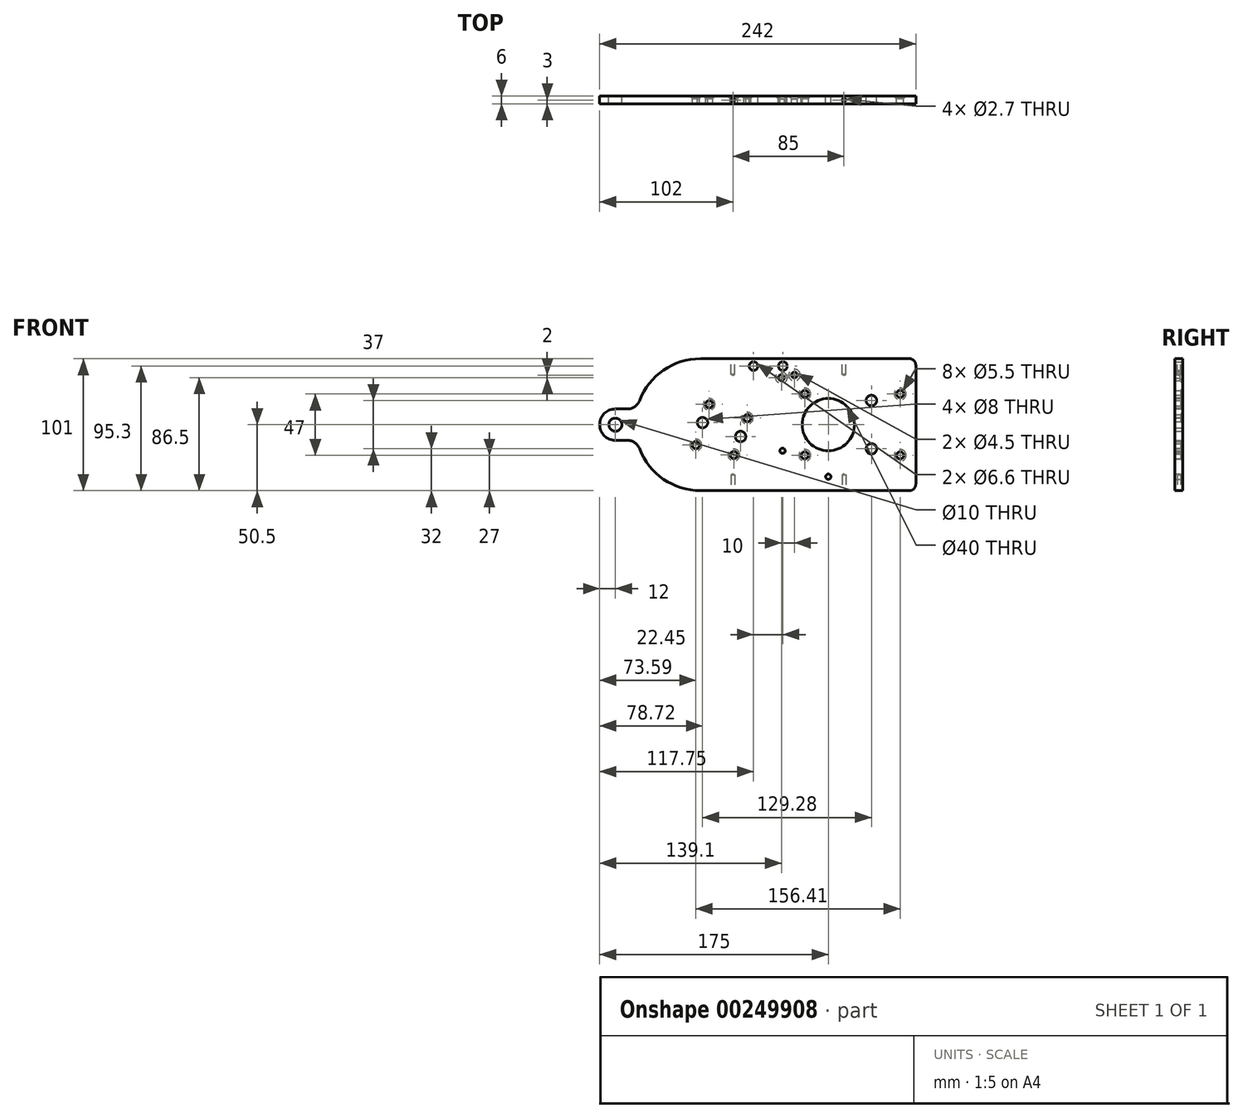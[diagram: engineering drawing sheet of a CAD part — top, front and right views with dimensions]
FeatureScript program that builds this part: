
annotation { "Feature Type Name" : "Feature", "Feature Type Description" : "" }
export const myFeature = defineFeature(function(context is Context, id is Id, definition is map)
    precondition{}
    {
        {
            var Q0;
            Q0=qCreatedBy(makeId("Front.planeOp"),FACE);
            var sketch = newSketch(context, id + "F0", { "sketchPlane" : qUnion([Q0])});
            skLineSegment(sketch, "E0.bottom", {"start": v(-115, -50.5) * mm, "end": v(115, -50.5) * mm});
            skLineSegment(sketch, "E0.top", {"start": v(-49.78, 50.5) * mm, "end": v(115, 50.5) * mm});
            skLineSegment(sketch, "E0.left", {"start": v(-115, -50.5) * mm, "end": v(-115, -12) * mm});
            skLineSegment(sketch, "E0.right", {"start": v(115, -50.5) * mm, "end": v(115, 50.5) * mm});
            skLineSegment(sketch, "E1", {"start": v(-162.21, 0) * mm, "end": v(164.39, 0) * mm, "construction": true});
            skPoint(sketch, "E1.endSnap0", {"position": v(115, 0) * mm});
            skCircle(sketch, "E2", {"center": v(-115, 0) * mm, "radius": 5 * mm});
            skArc(sketch, "E3", {"start": v(-115, 12) * mm, "mid": v(-127, 0) * mm, "end": v(-115, -12) * mm});
            skLineSegment(sketch, "E4", {"start": v(-115, 12) * mm, "end": v(-105.8, 12) * mm});
            skLineSegment(sketch, "E5", {"start": v(-115, -12) * mm, "end": v(-105.8, -12) * mm});
            skArc(sketch, "E6", {"start": v(-105.8, 12) * mm, "mid": v(-100.14, 13.76) * mm, "end": v(-96.46, 18.42) * mm});
            skArc(sketch, "E7", {"start": v(-96.46, 18.42) * mm, "mid": v(-78.1, 41.7) * mm, "end": v(-49.78, 50.5) * mm});
            skArc(sketch, "E8", {"start": v(-105.8, -12) * mm, "mid": v(-100.14, -13.76) * mm, "end": v(-96.46, -18.42) * mm});
            skArc(sketch, "E9", {"start": v(-96.46, -18.42) * mm, "mid": v(-78.1, -41.7) * mm, "end": v(-49.78, -50.5) * mm});
            skPoint(sketch, "E10.orphan", {"position": v(-115, 50.5) * mm});
            skCircle(sketch, "E11", {"center": v(48, 0) * mm, "radius": 20 * mm});
            skCircle(sketch, "E12", {"center": v(81, -18.5) * mm, "radius": 4 * mm});
            skCircle(sketch, "E13", {"center": v(81, 18.5) * mm, "radius": 4 * mm});
            skLineSegment(sketch, "E14", {"start": v(103, 65.88) * mm, "end": v(103, -57.13) * mm, "construction": true});
            skCircle(sketch, "E15", {"center": v(103, -23.5) * mm, "radius": 3.48 * mm});
            skCircle(sketch, "E16", {"center": v(103, 23.5) * mm, "radius": 3.5 * mm});
            skCircle(sketch, "E17", {"center": v(30, 23.5) * mm, "radius": 6.97 * mm});
            skCircle(sketch, "E18", {"center": v(30, -23.5) * mm, "radius": 11.5 * mm});
            skCircle(sketch, "E19", {"center": v(-48.28, 1.52) * mm, "radius": 4 * mm});
            skCircle(sketch, "E20", {"center": v(-19.15, -9.1) * mm, "radius": 4 * mm});
            skCircle(sketch, "E21", {"center": v(-14.02, 5) * mm, "radius": 5.47 * mm});
            skCircle(sketch, "E22", {"center": v(-24.28, -23.2) * mm, "radius": 5.45 * mm});
            skCircle(sketch, "E23", {"center": v(-43.15, 15.6) * mm, "radius": 4.25 * mm});
            skCircle(sketch, "E24", {"center": v(-53.41, -15.6) * mm, "radius": 6.02 * mm});
            skCircle(sketch, "E25", {"center": v(22.1, 38) * mm, "radius": 6.15 * mm});
            skCircle(sketch, "E26", {"center": v(12.1, 36) * mm, "radius": 7.66 * mm});
            skCircle(sketch, "E27", {"center": v(48, -39.8) * mm, "radius": 2 * mm});
            skCircle(sketch, "E28", {"center": v(13, -20) * mm, "radius": 2 * mm});
            skCircle(sketch, "E29", {"center": v(13.2, 44.8) * mm, "radius": 2.64 * mm});
            skCircle(sketch, "E30", {"center": v(-9.25, 44.8) * mm, "radius": 3.14 * mm});
            skSolve(sketch);
        }
        {
            var Q0;
            Q0=makeQuery(id+"F0.imprint","IMPRINT",FACE,{"disambiguationData":[TD([[makeQuery(id+"F0.imprint","IMPRINT",EDGE,{"derivedFrom":sQuery(id+"F0.wireOp",EDGE,"E0.top")}),-1.0]])]});
            var Q1;
            Q1=makeQuery(id+"F0.imprint","IMPRINT",FACE,{"disambiguationData":[TD([[makeQuery(id+"F0.imprint","IMPRINT",EDGE,{"derivedFrom":sQuery(id+"F0.wireOp",EDGE,"E23")}),1.0]])]});
            var Q2;
            Q2=makeQuery(id+"F0.imprint","IMPRINT",FACE,{"disambiguationData":[TD([[makeQuery(id+"F0.imprint","IMPRINT",EDGE,{"derivedFrom":sQuery(id+"F0.wireOp",EDGE,"E24")}),1.0]])]});
            var Q3;
            Q3=makeQuery(id+"F0.imprint","IMPRINT",FACE,{"disambiguationData":[TD([[makeQuery(id+"F0.imprint","IMPRINT",EDGE,{"derivedFrom":sQuery(id+"F0.wireOp",EDGE,"E21")}),1.0]])]});
            var Q4;
            Q4=makeQuery(id+"F0.imprint","IMPRINT",FACE,{"disambiguationData":[TD([[makeQuery(id+"F0.imprint","IMPRINT",EDGE,{"derivedFrom":sQuery(id+"F0.wireOp",EDGE,"E22")}),1.0]])]});
            var Q5;
            {var subQ0=sQuery(id+"F0.wireOp",EDGE,"E26");var subQ1=sQuery(id+"F0.wireOp",EDGE,"E25");var subQ2=makeQuery(id+"F0.imprint","INTERSECT",VERTEX,{"disambiguationData":[OD(0.0)],"derivedFrom":[subQ1,subQ0]});Q5=makeQuery(id+"F0.imprint","IMPRINT",FACE,{"disambiguationData":[TD([[makeQuery(id+"F0.imprint","IMPRINT",EDGE,{"disambiguationData":[TD([[subQ2,-1.0]])],"derivedFrom":subQ1}),-1.0]])]});}
            var Q6;
            {var subQ0=sQuery(id+"F0.wireOp",EDGE,"E26");var subQ1=sQuery(id+"F0.wireOp",EDGE,"E25");var subQ2=makeQuery(id+"F0.imprint","INTERSECT",VERTEX,{"disambiguationData":[OD(0.0)],"derivedFrom":[subQ1,subQ0]});Q6=makeQuery(id+"F0.imprint","IMPRINT",FACE,{"disambiguationData":[TD([[makeQuery(id+"F0.imprint","IMPRINT",EDGE,{"disambiguationData":[TD([[subQ2,1.0]])],"derivedFrom":subQ1}),1.0]])]});}
            var Q7;
            Q7=makeQuery(id+"F0.imprint","IMPRINT",FACE,{"disambiguationData":[TD([[makeQuery(id+"F0.imprint","IMPRINT",EDGE,{"derivedFrom":sQuery(id+"F0.wireOp",EDGE,"E17")}),1.0]])]});
            var Q8;
            {var subQ0=sQuery(id+"F0.wireOp",EDGE,"E18");var subQ1=sQuery(id+"F0.wireOp",EDGE,"E11");var subQ2=makeQuery(id+"F0.imprint","INTERSECT",VERTEX,{"disambiguationData":[OD(0.0)],"derivedFrom":[subQ1,subQ0]});Q8=makeQuery(id+"F0.imprint","IMPRINT",FACE,{"disambiguationData":[TD([[makeQuery(id+"F0.imprint","IMPRINT",EDGE,{"disambiguationData":[TD([[subQ2,-1.0]])],"derivedFrom":subQ1}),-1.0]])]});}
            var Q9;
            Q9=makeQuery(id+"F0.imprint","IMPRINT",FACE,{"disambiguationData":[TD([[makeQuery(id+"F0.imprint","IMPRINT",EDGE,{"derivedFrom":sQuery(id+"F0.wireOp",EDGE,"E16")}),1.0]])]});
            var Q10;
            Q10=makeQuery(id+"F0.imprint","IMPRINT",FACE,{"disambiguationData":[TD([[makeQuery(id+"F0.imprint","IMPRINT",EDGE,{"derivedFrom":sQuery(id+"F0.wireOp",EDGE,"E15")}),1.0]])]});
            var Q11;
            {var subQ0=sQuery(id+"F0.wireOp",EDGE,"E29");var subQ1=sQuery(id+"F0.wireOp",EDGE,"E26");var subQ2=makeQuery(id+"F0.imprint","INTERSECT",VERTEX,{"disambiguationData":[OD(0.0)],"derivedFrom":[subQ1,subQ0]});Q11=makeQuery(id+"F0.imprint","IMPRINT",FACE,{"disambiguationData":[TD([[makeQuery(id+"F0.imprint","IMPRINT",EDGE,{"disambiguationData":[TD([[subQ2,-1.0]])],"derivedFrom":subQ1}),-1.0]])]});}
            var Q12;
            {var subQ0=sQuery(id+"F0.wireOp",EDGE,"E29");var subQ1=sQuery(id+"F0.wireOp",EDGE,"E26");var subQ2=makeQuery(id+"F0.imprint","INTERSECT",VERTEX,{"disambiguationData":[OD(0.0)],"derivedFrom":[subQ1,subQ0]});Q12=makeQuery(id+"F0.imprint","IMPRINT",FACE,{"disambiguationData":[TD([[makeQuery(id+"F0.imprint","IMPRINT",EDGE,{"disambiguationData":[TD([[subQ2,-1.0]])],"derivedFrom":subQ1}),1.0]])]});}
            var Q13;
            Q13=makeQuery(id+"F0.imprint","IMPRINT",FACE,{"disambiguationData":[TD([[makeQuery(id+"F0.imprint","IMPRINT",EDGE,{"derivedFrom":sQuery(id+"F0.wireOp",EDGE,"E30")}),1.0]])]});
            var Q14;
            {var subQ0=sQuery(id+"F0.wireOp",EDGE,"E26");var subQ1=sQuery(id+"F0.wireOp",EDGE,"E25");var subQ2=makeQuery(id+"F0.imprint","INTERSECT",VERTEX,{"disambiguationData":[OD(0.0)],"derivedFrom":[subQ1,subQ0]});Q14=makeQuery(id+"F0.imprint","IMPRINT",FACE,{"disambiguationData":[TD([[makeQuery(id+"F0.imprint","IMPRINT",EDGE,{"disambiguationData":[TD([[subQ2,-1.0]])],"derivedFrom":subQ1}),1.0]])]});}
            extrude(context, id + "F1", {"entities" : qUnion([Q0, Q1, Q2, Q3, Q4, Q5, Q6, Q7, Q8, Q9, Q10, Q11, Q12, Q13, Q14]), "depth" : 6 * mm});
        }
        {
            var Q0;
            Q0=sQuery(id+"F0.wireOp",VERTEX,"E23.center");
            var Q1;
            Q1=sQuery(id+"F0.wireOp",VERTEX,"E24.center");
            var Q2;
            Q2=sQuery(id+"F0.wireOp",VERTEX,"E21.center");
            var Q3;
            Q3=sQuery(id+"F0.wireOp",VERTEX,"E22.center");
            var Q4;
            Q4=sQuery(id+"F0.wireOp",VERTEX,"E18.center");
            var Q5;
            Q5=sQuery(id+"F0.wireOp",VERTEX,"E17.center");
            var Q6;
            Q6=sQuery(id+"F0.wireOp",VERTEX,"E16.center");
            var Q7;
            Q7=sQuery(id+"F0.wireOp",VERTEX,"E15.center");
            var Q8;
            Q8=makeQuery(id+"F1.opExtrude","SWEPT_BODY",BODY,{"disambiguationData":[OSD([sQuery(id+"F0.wireOp",EDGE,"E0.bottom"),sQuery(id+"F0.wireOp",EDGE,"E0.top"),sQuery(id+"F0.wireOp",EDGE,"E0.right"),sQuery(id+"F0.wireOp",EDGE,"E2"),sQuery(id+"F0.wireOp",EDGE,"E3"),sQuery(id+"F0.wireOp",EDGE,"E4"),sQuery(id+"F0.wireOp",EDGE,"E5"),sQuery(id+"F0.wireOp",EDGE,"E6"),sQuery(id+"F0.wireOp",EDGE,"E7"),sQuery(id+"F0.wireOp",EDGE,"E8"),sQuery(id+"F0.wireOp",EDGE,"E9"),sQuery(id+"F0.wireOp",EDGE,"E11"),sQuery(id+"F0.wireOp",EDGE,"E12"),sQuery(id+"F0.wireOp",EDGE,"E13"),sQuery(id+"F0.wireOp",EDGE,"E19"),sQuery(id+"F0.wireOp",EDGE,"E20"),sQuery(id+"F0.wireOp",EDGE,"E27"),sQuery(id+"F0.wireOp",EDGE,"E28")])]});
            hole(context, id + "F2", {"style" : HoleStyle.C_SINK, "endStyle" : HoleEndStyle.THROUGH, "oppositeDirection" : true, "holeDiameter" : 5.5 * mm, "cSinkDiameter" : 8.96 * mm, "cSinkAngle" : 90 * degree, "tappedDepth" : 12 * mm, "tapClearance" : 3, "locations" : qUnion([Q0, Q1, Q2, Q3, Q4, Q5, Q6, Q7]), "scope" : qUnion([Q8])});
        }
        {
            var Q0;
            Q0=sQuery(id+"F0.wireOp",VERTEX,"E25.center");
            var Q1;
            Q1=sQuery(id+"F0.wireOp",VERTEX,"E26.center");
            var Q2;
            Q2=makeQuery(id+"F1.opExtrude","SWEPT_BODY",BODY,{"disambiguationData":[OSD([sQuery(id+"F0.wireOp",EDGE,"E0.bottom"),sQuery(id+"F0.wireOp",EDGE,"E0.top"),sQuery(id+"F0.wireOp",EDGE,"E0.right"),sQuery(id+"F0.wireOp",EDGE,"E2"),sQuery(id+"F0.wireOp",EDGE,"E3"),sQuery(id+"F0.wireOp",EDGE,"E4"),sQuery(id+"F0.wireOp",EDGE,"E5"),sQuery(id+"F0.wireOp",EDGE,"E6"),sQuery(id+"F0.wireOp",EDGE,"E7"),sQuery(id+"F0.wireOp",EDGE,"E8"),sQuery(id+"F0.wireOp",EDGE,"E9"),sQuery(id+"F0.wireOp",EDGE,"E11"),sQuery(id+"F0.wireOp",EDGE,"E12"),sQuery(id+"F0.wireOp",EDGE,"E13"),sQuery(id+"F0.wireOp",EDGE,"E19"),sQuery(id+"F0.wireOp",EDGE,"E20"),sQuery(id+"F0.wireOp",EDGE,"E27"),sQuery(id+"F0.wireOp",EDGE,"E28")])]});
            hole(context, id + "F3", {"style" : HoleStyle.C_SINK, "endStyle" : HoleEndStyle.THROUGH, "oppositeDirection" : true, "holeDiameter" : 4.5 * mm, "cSinkDiameter" : 8.96 * mm, "cSinkAngle" : 90 * degree, "tappedDepth" : 12 * mm, "tapClearance" : 3, "locations" : qUnion([Q0, Q1]), "scope" : qUnion([Q2])});
        }
        {
            var Q0;
            Q0=sQuery(id+"F0.wireOp",VERTEX,"E30.center");
            var Q1;
            Q1=sQuery(id+"F0.wireOp",VERTEX,"E29.center");
            var Q2;
            Q2=makeQuery(id+"F1.opExtrude","SWEPT_BODY",BODY,{"disambiguationData":[OSD([sQuery(id+"F0.wireOp",EDGE,"E0.bottom"),sQuery(id+"F0.wireOp",EDGE,"E0.top"),sQuery(id+"F0.wireOp",EDGE,"E0.right"),sQuery(id+"F0.wireOp",EDGE,"E2"),sQuery(id+"F0.wireOp",EDGE,"E3"),sQuery(id+"F0.wireOp",EDGE,"E4"),sQuery(id+"F0.wireOp",EDGE,"E5"),sQuery(id+"F0.wireOp",EDGE,"E6"),sQuery(id+"F0.wireOp",EDGE,"E7"),sQuery(id+"F0.wireOp",EDGE,"E8"),sQuery(id+"F0.wireOp",EDGE,"E9"),sQuery(id+"F0.wireOp",EDGE,"E11"),sQuery(id+"F0.wireOp",EDGE,"E12"),sQuery(id+"F0.wireOp",EDGE,"E13"),sQuery(id+"F0.wireOp",EDGE,"E19"),sQuery(id+"F0.wireOp",EDGE,"E20"),sQuery(id+"F0.wireOp",EDGE,"E27"),sQuery(id+"F0.wireOp",EDGE,"E28")])]});
            hole(context, id + "F4", {"style" : HoleStyle.SIMPLE, "endStyle" : HoleEndStyle.THROUGH, "oppositeDirection" : true, "standardTappedOrClearance" : lookupTablePath({ "standard" : "ISO", "fit" : "Normal", "size" : "M6", "type" : "Clearance" }), "standardBlindInLast" : lookupTablePath({ "fit" : "Standard", "standard" : "ISO", "size" : "M6", "type" : "Clearance" }), "holeDiameter" : 6.6 * mm, "tappedDepth" : 12 * mm, "tapClearance" : 3, "locations" : qUnion([Q0, Q1]), "scope" : qUnion([Q2])});
        }
        {
            var Q0;
            Q0=makeQuery(id+"F1.opExtrude","SWEPT_FACE",FACE,{"disambiguationData":[OSD([sQuery(id+"F0.wireOp",EDGE,"E0.bottom")])]});
            var sketch = newSketch(context, id + "F5", { "sketchPlane" : qUnion([Q0])});
            skLineSegment(sketch, "E31", {"start": v(-53.96, 3) * mm, "end": v(118.5, 3) * mm, "construction": true});
            skPoint(sketch, "E31.startSnap0", {"position": v(-49.78, 3) * mm});
            skPoint(sketch, "E32", {"position": v(60, 3) * mm});
            skPoint(sketch, "E33", {"position": v(-25, 3) * mm});
            skSolve(sketch);
        }
        {
            var Q0;
            Q0=sQuery(id+"F5.wireOp",VERTEX,"E32");
            var Q1;
            Q1=sQuery(id+"F5.wireOp",VERTEX,"E33");
            var Q2;
            Q2=makeQuery(id+"F1.opExtrude","SWEPT_BODY",BODY,{"disambiguationData":[OSD([sQuery(id+"F0.wireOp",EDGE,"E0.bottom"),sQuery(id+"F0.wireOp",EDGE,"E0.top"),sQuery(id+"F0.wireOp",EDGE,"E0.right"),sQuery(id+"F0.wireOp",EDGE,"E2"),sQuery(id+"F0.wireOp",EDGE,"E3"),sQuery(id+"F0.wireOp",EDGE,"E4"),sQuery(id+"F0.wireOp",EDGE,"E5"),sQuery(id+"F0.wireOp",EDGE,"E6"),sQuery(id+"F0.wireOp",EDGE,"E7"),sQuery(id+"F0.wireOp",EDGE,"E8"),sQuery(id+"F0.wireOp",EDGE,"E9"),sQuery(id+"F0.wireOp",EDGE,"E11"),sQuery(id+"F0.wireOp",EDGE,"E12"),sQuery(id+"F0.wireOp",EDGE,"E13"),sQuery(id+"F0.wireOp",EDGE,"E19"),sQuery(id+"F0.wireOp",EDGE,"E20"),sQuery(id+"F0.wireOp",EDGE,"E27"),sQuery(id+"F0.wireOp",EDGE,"E28")])]});
            hole(context, id + "F6", {"style" : HoleStyle.SIMPLE, "endStyle" : HoleEndStyle.BLIND, "holeDiameter" : 2.7 * mm, "holeDepth" : 12 * mm, "tappedDepth" : 12 * mm, "tapClearance" : 3, "locations" : qUnion([Q0, Q1]), "scope" : qUnion([Q2])});
        }
        {
            var Q0;
            Q0=makeQuery(id+"F1.opExtrude","SWEPT_FACE",FACE,{"disambiguationData":[OSD([sQuery(id+"F0.wireOp",EDGE,"E0.top")])]});
            var sketch = newSketch(context, id + "F7", { "sketchPlane" : qUnion([Q0])});
            skLineSegment(sketch, "E34", {"start": v(115, -3) * mm, "end": v(-65.1, -3) * mm, "construction": true});
            skPoint(sketch, "E35", {"position": v(60, -3) * mm});
            skPoint(sketch, "E36", {"position": v(-25, -3) * mm});
            skSolve(sketch);
        }
        {
            var Q0;
            Q0=sQuery(id+"F7.wireOp",VERTEX,"E36");
            var Q1;
            Q1=sQuery(id+"F7.wireOp",VERTEX,"E35");
            var Q2;
            Q2=makeQuery(id+"F1.opExtrude","SWEPT_BODY",BODY,{"disambiguationData":[OSD([sQuery(id+"F0.wireOp",EDGE,"E0.bottom"),sQuery(id+"F0.wireOp",EDGE,"E0.top"),sQuery(id+"F0.wireOp",EDGE,"E0.right"),sQuery(id+"F0.wireOp",EDGE,"E2"),sQuery(id+"F0.wireOp",EDGE,"E3"),sQuery(id+"F0.wireOp",EDGE,"E4"),sQuery(id+"F0.wireOp",EDGE,"E5"),sQuery(id+"F0.wireOp",EDGE,"E6"),sQuery(id+"F0.wireOp",EDGE,"E7"),sQuery(id+"F0.wireOp",EDGE,"E8"),sQuery(id+"F0.wireOp",EDGE,"E9"),sQuery(id+"F0.wireOp",EDGE,"E11"),sQuery(id+"F0.wireOp",EDGE,"E12"),sQuery(id+"F0.wireOp",EDGE,"E13"),sQuery(id+"F0.wireOp",EDGE,"E19"),sQuery(id+"F0.wireOp",EDGE,"E20"),sQuery(id+"F0.wireOp",EDGE,"E27"),sQuery(id+"F0.wireOp",EDGE,"E28")])]});
            hole(context, id + "F8", {"style" : HoleStyle.SIMPLE, "endStyle" : HoleEndStyle.BLIND, "holeDiameter" : 2.7 * mm, "holeDepth" : 12 * mm, "tappedDepth" : 12 * mm, "tapClearance" : 3, "locations" : qUnion([Q0, Q1]), "scope" : qUnion([Q2])});
        }
        {
            var Q0;
            Q0=makeQuery(id+"F1.opExtrude","SWEPT_EDGE",EDGE,{"disambiguationData":[OSD([sQuery(id+"F0.wireOp",EDGE,"E0.top"),sQuery(id+"F0.wireOp",EDGE,"E0.right")])]});
            var Q1;
            Q1=makeQuery(id+"F1.opExtrude","SWEPT_EDGE",EDGE,{"disambiguationData":[OSD([sQuery(id+"F0.wireOp",EDGE,"E0.bottom"),sQuery(id+"F0.wireOp",EDGE,"E0.right")])]});
            fillet(context, id + "F9", {"entities" : qUnion([Q0, Q1]), "radius" : 5 * mm, "tangentPropagation" : true, "allowEdgeOverflow" : false});
        }
    });
